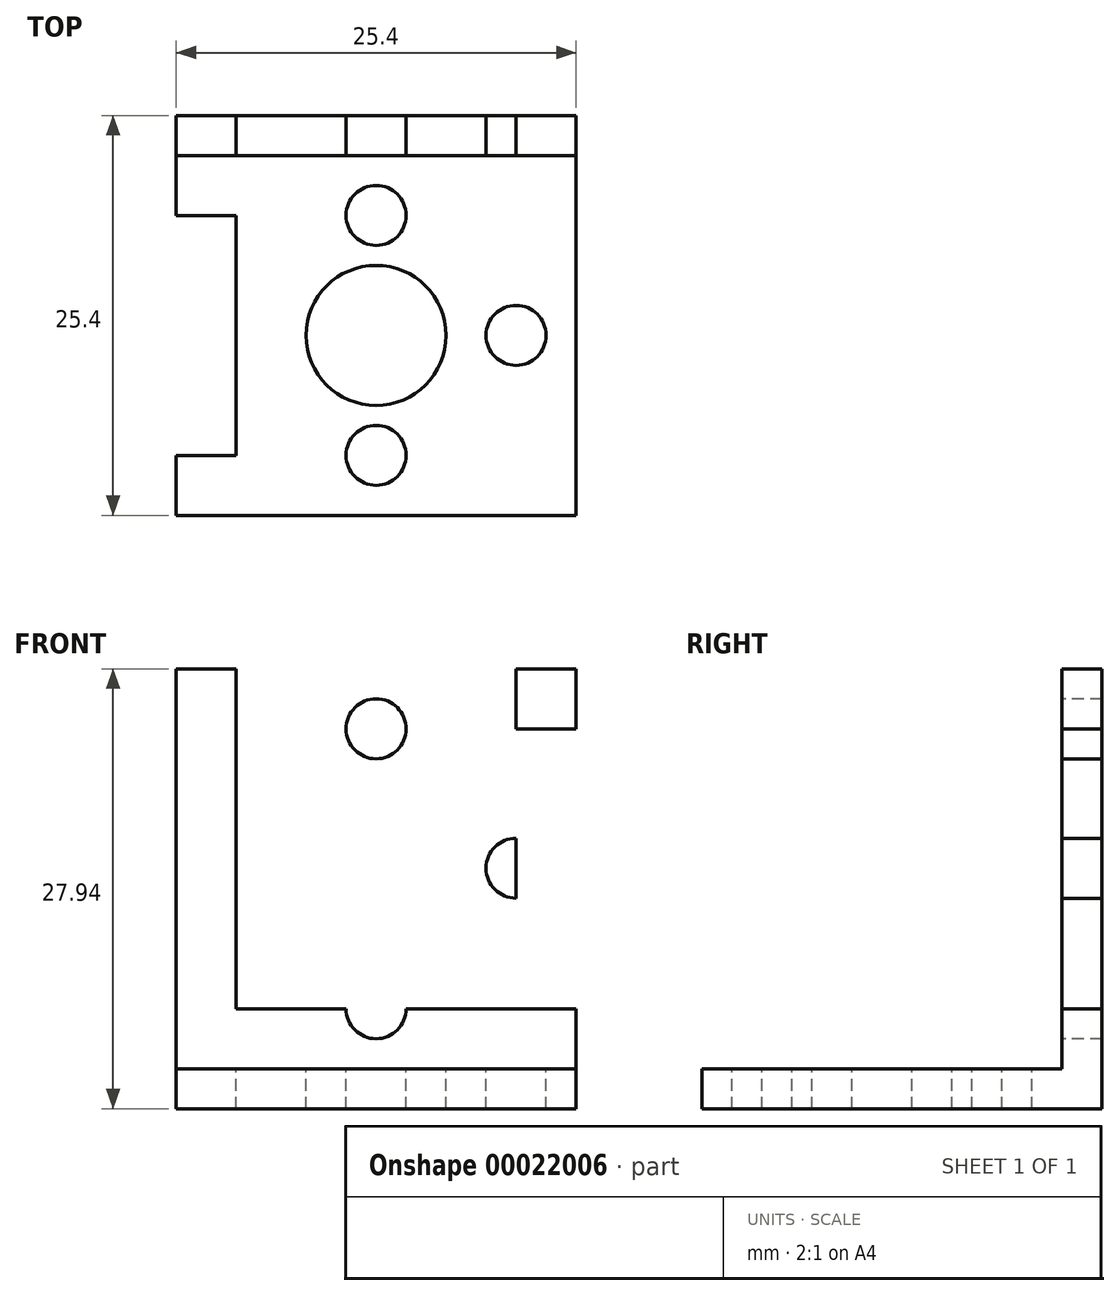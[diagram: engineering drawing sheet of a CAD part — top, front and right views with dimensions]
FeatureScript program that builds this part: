
annotation { "Feature Type Name" : "Feature", "Feature Type Description" : "" }
export const myFeature = defineFeature(function(context is Context, id is Id, definition is map)
    precondition{}
    {
        {
            var Q0;
            Q0=qCreatedBy(makeId("Front.planeOp"),FACE);
            var sketch = newSketch(context, id + "F0", { "sketchPlane" : qUnion([Q0])});
            skLineSegment(sketch, "E0.bottom", {"start": v(-42.85, -6.97) * mm, "end": v(-17.45, -6.97) * mm});
            skLineSegment(sketch, "E0.top", {"start": v(-42.85, -9.51) * mm, "end": v(-17.45, -9.51) * mm});
            skLineSegment(sketch, "E0.left", {"start": v(-42.85, -6.97) * mm, "end": v(-42.85, -9.51) * mm});
            skLineSegment(sketch, "E0.right", {"start": v(-17.45, -6.97) * mm, "end": v(-17.45, -9.51) * mm});
            skSolve(sketch);
        }
        {
            var Q0;
            Q0 = qSketchRegion(id + "F0", true);
            extrude(context, id + "F1", {"entities" : qUnion([Q0]), "depth" : 25.4 * mm});
        }
        {
            var Q0;
            Q0=makeQuery(id+"F1.opExtrude","SWEPT_FACE",FACE,{"disambiguationData":[OSD([sQuery(id+"F0.wireOp",EDGE,"E0.bottom")])]});
            var sketch = newSketch(context, id + "F2", { "sketchPlane" : qUnion([Q0])});
            skLineSegment(sketch, "E1.bottom", {"start": v(-42.85, 0) * mm, "end": v(-17.45, 0) * mm});
            skLineSegment(sketch, "E1.top", {"start": v(-42.85, -2.54) * mm, "end": v(-17.45, -2.54) * mm});
            skLineSegment(sketch, "E1.left", {"start": v(-42.85, 0) * mm, "end": v(-42.85, -2.54) * mm});
            skLineSegment(sketch, "E1.right", {"start": v(-17.45, 0) * mm, "end": v(-17.45, -2.54) * mm});
            skSolve(sketch);
        }
        {
            var Q0;
            Q0 = qSketchRegion(id + "F2", true);
            extrude(context, id + "F3", {"entities" : qUnion([Q0]), "operationType" : NewBodyOperationType.ADD, "depth" : 25.4 * mm});
        }
        {
            var Q0;
            Q0=makeQuery(id+"F1.opExtrude","SWEPT_FACE",FACE,{"disambiguationData":[OSD([sQuery(id+"F0.wireOp",EDGE,"E0.bottom")])]});
            var sketch = newSketch(context, id + "F4", { "sketchPlane" : qUnion([Q0])});
            skLineSegment(sketch, "E2", {"start": v(-30.15, -13.97) * mm, "end": v(-42.85, -13.97) * mm});
            skLineSegment(sketch, "E3", {"start": v(-30.15, -13.97) * mm, "end": v(-17.45, -13.97) * mm});
            skLineSegment(sketch, "E4", {"start": v(-30.15, -13.97) * mm, "end": v(-30.15, -2.54) * mm});
            skLineSegment(sketch, "E5", {"start": v(-30.15, -13.97) * mm, "end": v(-30.15, -25.4) * mm});
            skLineSegment(sketch, "E6", {"start": v(-42.85, -25.4) * mm, "end": v(-39.04, -25.4) * mm});
            skLineSegment(sketch, "E7", {"start": v(-42.85, -25.4) * mm, "end": v(-42.85, -21.59) * mm});
            skLineSegment(sketch, "E8", {"start": v(-42.85, -21.59) * mm, "end": v(-17.45, -21.59) * mm});
            skLineSegment(sketch, "E9", {"start": v(-39.04, -25.4) * mm, "end": v(-39.04, -2.54) * mm});
            skLineSegment(sketch, "E10", {"start": v(-42.85, -2.54) * mm, "end": v(-42.85, -6.35) * mm});
            skLineSegment(sketch, "E11", {"start": v(-42.85, -6.35) * mm, "end": v(-17.45, -6.35) * mm});
            skLineSegment(sketch, "E12", {"start": v(-17.45, -25.4) * mm, "end": v(-21.26, -25.4) * mm});
            skLineSegment(sketch, "E13", {"start": v(-21.26, -25.4) * mm, "end": v(-21.26, -2.54) * mm});
            skCircle(sketch, "E14", {"center": v(-30.15, -6.35) * mm, "radius": 1.9 * mm});
            skCircle(sketch, "E15", {"center": v(-30.15, -21.59) * mm, "radius": 1.9 * mm});
            skCircle(sketch, "E16", {"center": v(-21.26, -13.97) * mm, "radius": 1.9 * mm});
            skCircle(sketch, "E17", {"center": v(-39.04, -13.97) * mm, "radius": 1.9 * mm});
            skCircle(sketch, "E18", {"center": v(-30.15, -13.97) * mm, "radius": 4.45 * mm});
            skSolve(sketch);
        }
        {
            var Q0;
            {var subQ0=sQuery(id+"F4.wireOp",EDGE,"E14");var subQ3=sQuery(id+"F4.wireOp",EDGE,"E4");var subQ4=makeQuery(id+"F4.imprint","INTERSECT",VERTEX,{"disambiguationData":[OD(0.0)],"derivedFrom":[subQ3,subQ0]});Q0=makeQuery(id+"F4.imprint","IMPRINT",FACE,{"disambiguationData":[TD([[makeQuery(id+"F4.imprint","IMPRINT",EDGE,{"disambiguationData":[TD([[subQ4,-1.0]])],"derivedFrom":subQ3}),1.0]])]});}
            var Q1;
            {var subQ1=sQuery(id+"F4.wireOp",EDGE,"E11");var subQ3=sQuery(id+"F4.wireOp",EDGE,"E4");var subQ5=makeQuery(id+"F4.imprint","INTERSECT",VERTEX,{"derivedFrom":[subQ3,subQ1]});Q1=makeQuery(id+"F4.imprint","IMPRINT",FACE,{"disambiguationData":[TD([[makeQuery(id+"F4.imprint","IMPRINT",EDGE,{"disambiguationData":[TD([[subQ5,-1.0]])],"derivedFrom":subQ3}),1.0]])]});}
            var Q2;
            {var subQ1=sQuery(id+"F4.wireOp",EDGE,"E11");var subQ3=sQuery(id+"F4.wireOp",EDGE,"E4");var subQ5=makeQuery(id+"F4.imprint","INTERSECT",VERTEX,{"derivedFrom":[subQ3,subQ1]});Q2=makeQuery(id+"F4.imprint","IMPRINT",FACE,{"disambiguationData":[TD([[makeQuery(id+"F4.imprint","IMPRINT",EDGE,{"disambiguationData":[TD([[subQ5,-1.0]])],"derivedFrom":subQ3}),-1.0]])]});}
            var Q3;
            {var subQ1=sQuery(id+"F4.wireOp",EDGE,"E14");var subQ3=sQuery(id+"F4.wireOp",EDGE,"E4");var subQ5=makeQuery(id+"F4.imprint","INTERSECT",VERTEX,{"disambiguationData":[OD(0.0)],"derivedFrom":[subQ3,subQ1]});Q3=makeQuery(id+"F4.imprint","IMPRINT",FACE,{"disambiguationData":[TD([[makeQuery(id+"F4.imprint","IMPRINT",EDGE,{"disambiguationData":[TD([[subQ5,-1.0]])],"derivedFrom":subQ3}),-1.0]])]});}
            var Q4;
            {var subQ1=sQuery(id+"F4.wireOp",EDGE,"E18");var subQ3=sQuery(id+"F4.wireOp",EDGE,"E3");var subQ5=makeQuery(id+"F4.imprint","INTERSECT",VERTEX,{"derivedFrom":[subQ3,subQ1]});Q4=makeQuery(id+"F4.imprint","IMPRINT",FACE,{"disambiguationData":[TD([[makeQuery(id+"F4.imprint","IMPRINT",EDGE,{"disambiguationData":[TD([[subQ5,-1.0]])],"derivedFrom":subQ1}),1.0]])]});}
            var Q5;
            {var subQ0=sQuery(id+"F4.wireOp",EDGE,"E18");var subQ3=sQuery(id+"F4.wireOp",EDGE,"E3");var subQ4=makeQuery(id+"F4.imprint","INTERSECT",VERTEX,{"derivedFrom":[subQ3,subQ0]});Q5=makeQuery(id+"F4.imprint","IMPRINT",FACE,{"disambiguationData":[TD([[makeQuery(id+"F4.imprint","IMPRINT",EDGE,{"disambiguationData":[TD([[subQ4,1.0]])],"derivedFrom":subQ0}),1.0]])]});}
            var Q6;
            {var subQ0=sQuery(id+"F4.wireOp",EDGE,"E18");var subQ3=sQuery(id+"F4.wireOp",EDGE,"E2");var subQ4=makeQuery(id+"F4.imprint","INTERSECT",VERTEX,{"derivedFrom":[subQ3,subQ0]});Q6=makeQuery(id+"F4.imprint","IMPRINT",FACE,{"disambiguationData":[TD([[makeQuery(id+"F4.imprint","IMPRINT",EDGE,{"disambiguationData":[TD([[subQ4,-1.0]])],"derivedFrom":subQ0}),1.0]])]});}
            var Q7;
            {var subQ0=sQuery(id+"F4.wireOp",EDGE,"E18");var subQ3=sQuery(id+"F4.wireOp",EDGE,"E2");var subQ4=makeQuery(id+"F4.imprint","INTERSECT",VERTEX,{"derivedFrom":[subQ3,subQ0]});Q7=makeQuery(id+"F4.imprint","IMPRINT",FACE,{"disambiguationData":[TD([[makeQuery(id+"F4.imprint","IMPRINT",EDGE,{"disambiguationData":[TD([[subQ4,1.0]])],"derivedFrom":subQ0}),1.0]])]});}
            var Q8;
            {var subQ0=sQuery(id+"F4.wireOp",EDGE,"E17");var subQ3=sQuery(id+"F4.wireOp",EDGE,"E2");var subQ4=makeQuery(id+"F4.imprint","INTERSECT",VERTEX,{"disambiguationData":[OD(0.0)],"derivedFrom":[subQ3,subQ0]});Q8=makeQuery(id+"F4.imprint","IMPRINT",FACE,{"disambiguationData":[TD([[makeQuery(id+"F4.imprint","IMPRINT",EDGE,{"disambiguationData":[TD([[subQ4,-1.0]])],"derivedFrom":subQ3}),-1.0]])]});}
            var Q9;
            {var subQ1=sQuery(id+"F4.wireOp",EDGE,"E9");var subQ3=sQuery(id+"F4.wireOp",EDGE,"E2");var subQ5=makeQuery(id+"F4.imprint","INTERSECT",VERTEX,{"derivedFrom":[subQ3,subQ1]});Q9=makeQuery(id+"F4.imprint","IMPRINT",FACE,{"disambiguationData":[TD([[makeQuery(id+"F4.imprint","IMPRINT",EDGE,{"disambiguationData":[TD([[subQ5,-1.0]])],"derivedFrom":subQ3}),-1.0]])]});}
            var Q10;
            {var subQ0=sQuery(id+"F4.wireOp",EDGE,"E9");var subQ3=sQuery(id+"F4.wireOp",EDGE,"E2");var subQ4=makeQuery(id+"F4.imprint","INTERSECT",VERTEX,{"derivedFrom":[subQ3,subQ0]});Q10=makeQuery(id+"F4.imprint","IMPRINT",FACE,{"disambiguationData":[TD([[makeQuery(id+"F4.imprint","IMPRINT",EDGE,{"disambiguationData":[TD([[subQ4,-1.0]])],"derivedFrom":subQ3}),1.0]])]});}
            var Q11;
            {var subQ0=sQuery(id+"F4.wireOp",EDGE,"E17");var subQ3=sQuery(id+"F4.wireOp",EDGE,"E2");var subQ4=makeQuery(id+"F4.imprint","INTERSECT",VERTEX,{"disambiguationData":[OD(0.0)],"derivedFrom":[subQ3,subQ0]});Q11=makeQuery(id+"F4.imprint","IMPRINT",FACE,{"disambiguationData":[TD([[makeQuery(id+"F4.imprint","IMPRINT",EDGE,{"disambiguationData":[TD([[subQ4,-1.0]])],"derivedFrom":subQ3}),1.0]])]});}
            var Q12;
            {var subQ1=sQuery(id+"F4.wireOp",EDGE,"E8");var subQ3=sQuery(id+"F4.wireOp",EDGE,"E5");var subQ5=makeQuery(id+"F4.imprint","INTERSECT",VERTEX,{"derivedFrom":[subQ3,subQ1]});Q12=makeQuery(id+"F4.imprint","IMPRINT",FACE,{"disambiguationData":[TD([[makeQuery(id+"F4.imprint","IMPRINT",EDGE,{"disambiguationData":[TD([[subQ5,-1.0]])],"derivedFrom":subQ3}),-1.0]])]});}
            var Q13;
            {var subQ0=sQuery(id+"F4.wireOp",EDGE,"E15");var subQ3=sQuery(id+"F4.wireOp",EDGE,"E5");var subQ4=makeQuery(id+"F4.imprint","INTERSECT",VERTEX,{"disambiguationData":[OD(0.0)],"derivedFrom":[subQ3,subQ0]});Q13=makeQuery(id+"F4.imprint","IMPRINT",FACE,{"disambiguationData":[TD([[makeQuery(id+"F4.imprint","IMPRINT",EDGE,{"disambiguationData":[TD([[subQ4,-1.0]])],"derivedFrom":subQ3}),-1.0]])]});}
            var Q14;
            {var subQ0=sQuery(id+"F4.wireOp",EDGE,"E15");var subQ3=sQuery(id+"F4.wireOp",EDGE,"E5");var subQ4=makeQuery(id+"F4.imprint","INTERSECT",VERTEX,{"disambiguationData":[OD(0.0)],"derivedFrom":[subQ3,subQ0]});Q14=makeQuery(id+"F4.imprint","IMPRINT",FACE,{"disambiguationData":[TD([[makeQuery(id+"F4.imprint","IMPRINT",EDGE,{"disambiguationData":[TD([[subQ4,-1.0]])],"derivedFrom":subQ3}),1.0]])]});}
            var Q15;
            {var subQ0=sQuery(id+"F4.wireOp",EDGE,"E8");var subQ3=sQuery(id+"F4.wireOp",EDGE,"E5");var subQ4=makeQuery(id+"F4.imprint","INTERSECT",VERTEX,{"derivedFrom":[subQ3,subQ0]});Q15=makeQuery(id+"F4.imprint","IMPRINT",FACE,{"disambiguationData":[TD([[makeQuery(id+"F4.imprint","IMPRINT",EDGE,{"disambiguationData":[TD([[subQ4,-1.0]])],"derivedFrom":subQ3}),1.0]])]});}
            var Q16;
            {var subQ0=sQuery(id+"F4.wireOp",EDGE,"E16");var subQ3=sQuery(id+"F4.wireOp",EDGE,"E3");var subQ4=makeQuery(id+"F4.imprint","INTERSECT",VERTEX,{"disambiguationData":[OD(0.0)],"derivedFrom":[subQ3,subQ0]});Q16=makeQuery(id+"F4.imprint","IMPRINT",FACE,{"disambiguationData":[TD([[makeQuery(id+"F4.imprint","IMPRINT",EDGE,{"disambiguationData":[TD([[subQ4,-1.0]])],"derivedFrom":subQ3}),-1.0]])]});}
            var Q17;
            {var subQ1=sQuery(id+"F4.wireOp",EDGE,"E13");var subQ3=sQuery(id+"F4.wireOp",EDGE,"E3");var subQ5=makeQuery(id+"F4.imprint","INTERSECT",VERTEX,{"derivedFrom":[subQ3,subQ1]});Q17=makeQuery(id+"F4.imprint","IMPRINT",FACE,{"disambiguationData":[TD([[makeQuery(id+"F4.imprint","IMPRINT",EDGE,{"disambiguationData":[TD([[subQ5,-1.0]])],"derivedFrom":subQ3}),-1.0]])]});}
            var Q18;
            {var subQ1=sQuery(id+"F4.wireOp",EDGE,"E13");var subQ3=sQuery(id+"F4.wireOp",EDGE,"E3");var subQ5=makeQuery(id+"F4.imprint","INTERSECT",VERTEX,{"derivedFrom":[subQ3,subQ1]});Q18=makeQuery(id+"F4.imprint","IMPRINT",FACE,{"disambiguationData":[TD([[makeQuery(id+"F4.imprint","IMPRINT",EDGE,{"disambiguationData":[TD([[subQ5,-1.0]])],"derivedFrom":subQ3}),1.0]])]});}
            var Q19;
            {var subQ1=sQuery(id+"F4.wireOp",EDGE,"E16");var subQ3=sQuery(id+"F4.wireOp",EDGE,"E3");var subQ5=makeQuery(id+"F4.imprint","INTERSECT",VERTEX,{"disambiguationData":[OD(0.0)],"derivedFrom":[subQ3,subQ1]});Q19=makeQuery(id+"F4.imprint","IMPRINT",FACE,{"disambiguationData":[TD([[makeQuery(id+"F4.imprint","IMPRINT",EDGE,{"disambiguationData":[TD([[subQ5,-1.0]])],"derivedFrom":subQ3}),1.0]])]});}
            extrude(context, id + "F5", {"entities" : qUnion([Q0, Q1, Q2, Q3, Q4, Q5, Q6, Q7, Q8, Q9, Q10, Q11, Q12, Q13, Q14, Q15, Q16, Q17, Q18, Q19]), "operationType" : NewBodyOperationType.REMOVE, "oppositeDirection" : true, "depth" : 25.4 * mm});
        }
        {
            var Q0;
            Q0=makeQuery(id+"F3.opExtrude","SWEPT_FACE",FACE,{"disambiguationData":[OSD([sQuery(id+"F2.wireOp",EDGE,"E1.top")])]});
            var sketch = newSketch(context, id + "F6", { "sketchPlane" : qUnion([Q0])});
            skLineSegment(sketch, "E19", {"start": v(-42.85, 5.73) * mm, "end": v(-17.45, 5.73) * mm});
            skLineSegment(sketch, "E20", {"start": v(-21.26, 5.76) * mm, "end": v(-21.26, 18.43) * mm});
            skLineSegment(sketch, "E21", {"start": v(-21.26, 5.76) * mm, "end": v(-21.26, -6.97) * mm});
            skCircle(sketch, "E22", {"center": v(-21.26, 5.76) * mm, "radius": 1.9 * mm});
            skCircle(sketch, "E23", {"center": v(-39.04, 5.73) * mm, "radius": 1.9 * mm});
            skCircle(sketch, "E24", {"center": v(-30.15, -3.16) * mm, "radius": 1.9 * mm});
            skCircle(sketch, "E25", {"center": v(-30.15, 5.73) * mm, "radius": 4.45 * mm});
            skLineSegment(sketch, "E26", {"start": v(-21.26, 18.43) * mm, "end": v(-17.45, 18.43) * mm});
            skLineSegment(sketch, "E27", {"start": v(-42.85, 18.43) * mm, "end": v(-39.04, 18.43) * mm});
            skLineSegment(sketch, "E28", {"start": v(-39.04, 18.43) * mm, "end": v(-39.04, -6.97) * mm});
            skLineSegment(sketch, "E29", {"start": v(-42.85, 18.43) * mm, "end": v(-42.85, 14.62) * mm});
            skLineSegment(sketch, "E30", {"start": v(-42.85, 14.62) * mm, "end": v(-17.45, 14.62) * mm});
            skLineSegment(sketch, "E31", {"start": v(-42.85, -6.97) * mm, "end": v(-42.85, -3.16) * mm});
            skLineSegment(sketch, "E32", {"start": v(-42.85, -3.16) * mm, "end": v(-17.45, -3.16) * mm});
            skCircle(sketch, "E33", {"center": v(-30.15, 14.62) * mm, "radius": 1.9 * mm});
            skSolve(sketch);
        }
        {
            var Q0;
            {var subQ1=sQuery(id+"F6.wireOp",EDGE,"E23");var subQ3=sQuery(id+"F6.wireOp",EDGE,"E19");var subQ5=makeQuery(id+"F6.imprint","INTERSECT",VERTEX,{"disambiguationData":[OD(0.0)],"derivedFrom":[subQ3,subQ1]});Q0=makeQuery(id+"F6.imprint","IMPRINT",FACE,{"disambiguationData":[TD([[makeQuery(id+"F6.imprint","IMPRINT",EDGE,{"disambiguationData":[TD([[subQ5,-1.0]])],"derivedFrom":subQ3}),1.0]])]});}
            var Q1;
            {var subQ0=sQuery(id+"F6.wireOp",EDGE,"E28");var subQ3=sQuery(id+"F6.wireOp",EDGE,"E19");var subQ4=makeQuery(id+"F6.imprint","INTERSECT",VERTEX,{"derivedFrom":[subQ3,subQ0]});Q1=makeQuery(id+"F6.imprint","IMPRINT",FACE,{"disambiguationData":[TD([[makeQuery(id+"F6.imprint","IMPRINT",EDGE,{"disambiguationData":[TD([[subQ4,-1.0]])],"derivedFrom":subQ3}),1.0]])]});}
            var Q2;
            {var subQ0=sQuery(id+"F6.wireOp",EDGE,"E28");var subQ3=sQuery(id+"F6.wireOp",EDGE,"E19");var subQ4=makeQuery(id+"F6.imprint","INTERSECT",VERTEX,{"derivedFrom":[subQ3,subQ0]});Q2=makeQuery(id+"F6.imprint","IMPRINT",FACE,{"disambiguationData":[TD([[makeQuery(id+"F6.imprint","IMPRINT",EDGE,{"disambiguationData":[TD([[subQ4,-1.0]])],"derivedFrom":subQ3}),-1.0]])]});}
            var Q3;
            {var subQ0=sQuery(id+"F6.wireOp",EDGE,"E23");var subQ3=sQuery(id+"F6.wireOp",EDGE,"E19");var subQ4=makeQuery(id+"F6.imprint","INTERSECT",VERTEX,{"disambiguationData":[OD(0.0)],"derivedFrom":[subQ3,subQ0]});Q3=makeQuery(id+"F6.imprint","IMPRINT",FACE,{"disambiguationData":[TD([[makeQuery(id+"F6.imprint","IMPRINT",EDGE,{"disambiguationData":[TD([[subQ4,-1.0]])],"derivedFrom":subQ3}),-1.0]])]});}
            var Q4;
            {var subQ0=sQuery(id+"F6.wireOp",EDGE,"E33");var subQ1=sQuery(id+"F6.wireOp",EDGE,"E30");var subQ3=makeQuery(id+"F6.imprint","INTERSECT",VERTEX,{"disambiguationData":[OD(0.0)],"derivedFrom":[subQ1,subQ0]});Q4=makeQuery(id+"F6.imprint","IMPRINT",FACE,{"disambiguationData":[TD([[makeQuery(id+"F6.imprint","IMPRINT",EDGE,{"disambiguationData":[TD([[subQ3,-1.0]])],"derivedFrom":subQ1}),-1.0]])]});}
            var Q5;
            {var subQ0=sQuery(id+"F6.wireOp",EDGE,"E33");var subQ1=sQuery(id+"F6.wireOp",EDGE,"E30");var subQ3=makeQuery(id+"F6.imprint","INTERSECT",VERTEX,{"disambiguationData":[OD(0.0)],"derivedFrom":[subQ1,subQ0]});Q5=makeQuery(id+"F6.imprint","IMPRINT",FACE,{"disambiguationData":[TD([[makeQuery(id+"F6.imprint","IMPRINT",EDGE,{"disambiguationData":[TD([[subQ3,-1.0]])],"derivedFrom":subQ1}),1.0]])]});}
            var Q6;
            {var subQ3=sQuery(id+"F6.wireOp",EDGE,"E19");var subQ5=sQuery(id+"F6.wireOp",EDGE,"E21");var subQ6=makeQuery(id+"F6.imprint","INTERSECT",VERTEX,{"derivedFrom":[subQ3,subQ5]});Q6=makeQuery(id+"F6.imprint","IMPRINT",FACE,{"disambiguationData":[TD([[makeQuery(id+"F6.imprint","IMPRINT",EDGE,{"disambiguationData":[TD([[subQ6,-1.0]])],"derivedFrom":subQ3}),1.0]])]});}
            var Q7;
            {var subQ0=sQuery(id+"F6.wireOp",EDGE,"E22");var subQ3=sQuery(id+"F6.wireOp",EDGE,"E19");var subQ4=makeQuery(id+"F6.imprint","INTERSECT",VERTEX,{"disambiguationData":[OD(0.0)],"derivedFrom":[subQ3,subQ0]});Q7=makeQuery(id+"F6.imprint","IMPRINT",FACE,{"disambiguationData":[TD([[makeQuery(id+"F6.imprint","IMPRINT",EDGE,{"disambiguationData":[TD([[subQ4,-1.0]])],"derivedFrom":subQ3}),1.0]])]});}
            var Q8;
            {var subQ0=sQuery(id+"F6.wireOp",EDGE,"E22");var subQ3=sQuery(id+"F6.wireOp",EDGE,"E19");var subQ4=makeQuery(id+"F6.imprint","INTERSECT",VERTEX,{"disambiguationData":[OD(0.0)],"derivedFrom":[subQ3,subQ0]});Q8=makeQuery(id+"F6.imprint","IMPRINT",FACE,{"disambiguationData":[TD([[makeQuery(id+"F6.imprint","IMPRINT",EDGE,{"disambiguationData":[TD([[subQ4,-1.0]])],"derivedFrom":subQ3}),-1.0]])]});}
            var Q9;
            {var subQ1=sQuery(id+"F6.wireOp",EDGE,"E21");var subQ3=sQuery(id+"F6.wireOp",EDGE,"E19");var subQ5=makeQuery(id+"F6.imprint","INTERSECT",VERTEX,{"derivedFrom":[subQ3,subQ1]});Q9=makeQuery(id+"F6.imprint","IMPRINT",FACE,{"disambiguationData":[TD([[makeQuery(id+"F6.imprint","IMPRINT",EDGE,{"disambiguationData":[TD([[subQ5,-1.0]])],"derivedFrom":subQ3}),-1.0]])]});}
            var Q10;
            {var subQ0=sQuery(id+"F6.wireOp",EDGE,"E32");var subQ1=sQuery(id+"F6.wireOp",EDGE,"E24");var subQ3=makeQuery(id+"F6.imprint","INTERSECT",VERTEX,{"disambiguationData":[OD(0.0)],"derivedFrom":[subQ1,subQ0]});Q10=makeQuery(id+"F6.imprint","IMPRINT",FACE,{"disambiguationData":[TD([[makeQuery(id+"F6.imprint","IMPRINT",EDGE,{"disambiguationData":[TD([[subQ3,1.0]])],"derivedFrom":subQ1}),1.0]])]});}
            var Q11;
            {var subQ0=sQuery(id+"F6.wireOp",EDGE,"E32");var subQ1=sQuery(id+"F6.wireOp",EDGE,"E24");var subQ3=makeQuery(id+"F6.imprint","INTERSECT",VERTEX,{"disambiguationData":[OD(0.0)],"derivedFrom":[subQ1,subQ0]});Q11=makeQuery(id+"F6.imprint","IMPRINT",FACE,{"disambiguationData":[TD([[makeQuery(id+"F6.imprint","IMPRINT",EDGE,{"disambiguationData":[TD([[subQ3,-1.0]])],"derivedFrom":subQ1}),1.0]])]});}
            var Q12;
            {var subQ0=sQuery(id+"F6.wireOp",EDGE,"E25");var subQ1=sQuery(id+"F6.wireOp",EDGE,"E19");var subQ3=makeQuery(id+"F6.imprint","INTERSECT",VERTEX,{"disambiguationData":[OD(0.0)],"derivedFrom":[subQ1,subQ0]});Q12=makeQuery(id+"F6.imprint","IMPRINT",FACE,{"disambiguationData":[TD([[makeQuery(id+"F6.imprint","IMPRINT",EDGE,{"disambiguationData":[TD([[subQ3,-1.0]])],"derivedFrom":subQ1}),-1.0]])]});}
            var Q13;
            {var subQ0=sQuery(id+"F6.wireOp",EDGE,"E25");var subQ1=sQuery(id+"F6.wireOp",EDGE,"E19");var subQ3=makeQuery(id+"F6.imprint","INTERSECT",VERTEX,{"disambiguationData":[OD(0.0)],"derivedFrom":[subQ1,subQ0]});Q13=makeQuery(id+"F6.imprint","IMPRINT",FACE,{"disambiguationData":[TD([[makeQuery(id+"F6.imprint","IMPRINT",EDGE,{"disambiguationData":[TD([[subQ3,-1.0]])],"derivedFrom":subQ1}),1.0]])]});}
            extrude(context, id + "F7", {"entities" : qUnion([Q0, Q1, Q2, Q3, Q4, Q5, Q6, Q7, Q8, Q9, Q10, Q11, Q12, Q13]), "operationType" : NewBodyOperationType.REMOVE, "oppositeDirection" : true, "depth" : 25.4 * mm});
        }
    });
